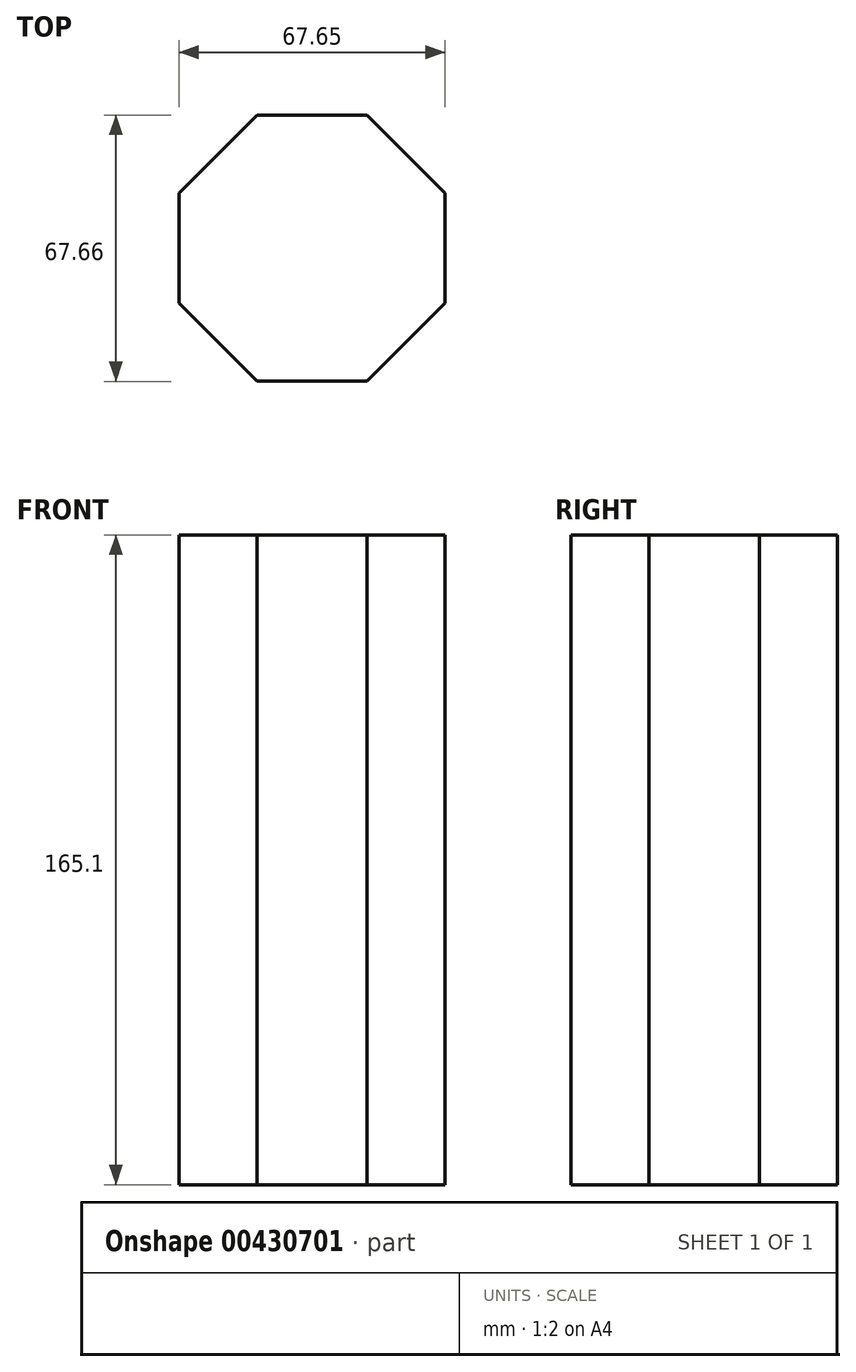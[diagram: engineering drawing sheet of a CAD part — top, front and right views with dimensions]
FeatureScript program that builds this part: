
annotation { "Feature Type Name" : "Feature", "Feature Type Description" : "" }
export const myFeature = defineFeature(function(context is Context, id is Id, definition is map)
    precondition{}
    {
        {
            var Q0;
            Q0=qCreatedBy(makeId("Top.planeOp"),FACE);
            var sketch = newSketch(context, id + "F0", { "sketchPlane" : qUnion([Q0])});
            skLineSegment(sketch, "E0.0", {"start": v(0, 14.01) * mm, "end": v(0, -14.01) * mm});
            skLineSegment(sketch, "E0.1", {"start": v(0, -14.01) * mm, "end": v(-19.81, -33.83) * mm});
            skLineSegment(sketch, "E0.2", {"start": v(-19.81, -33.83) * mm, "end": v(-47.84, -33.83) * mm});
            skLineSegment(sketch, "E0.3", {"start": v(-47.84, -33.83) * mm, "end": v(-67.65, -14.01) * mm});
            skLineSegment(sketch, "E0.4", {"start": v(-67.65, -14.01) * mm, "end": v(-67.65, 14.01) * mm});
            skLineSegment(sketch, "E0.5", {"start": v(-67.65, 14.01) * mm, "end": v(-47.84, 33.83) * mm});
            skLineSegment(sketch, "E0.6", {"start": v(-47.84, 33.83) * mm, "end": v(-19.81, 33.83) * mm});
            skLineSegment(sketch, "E0.7", {"start": v(-19.81, 33.83) * mm, "end": v(0, 14.01) * mm});
            skPoint(sketch, "E0.0.midPoint", {"position": v(0, 0) * mm});
            skSolve(sketch);
        }
        {
            var Q0;
            Q0=makeQuery(id+"F0.imprint","IMPRINT",FACE,{"disambiguationData":[TD([[makeQuery(id+"F0.imprint","IMPRINT",EDGE,{"derivedFrom":sQuery(id+"F0.wireOp",EDGE,"E0.0")}),-1.0]])]});
            extrude(context, id + "F1", {"entities" : qUnion([Q0]), "depth" : 165.1 * mm});
        }
    });
